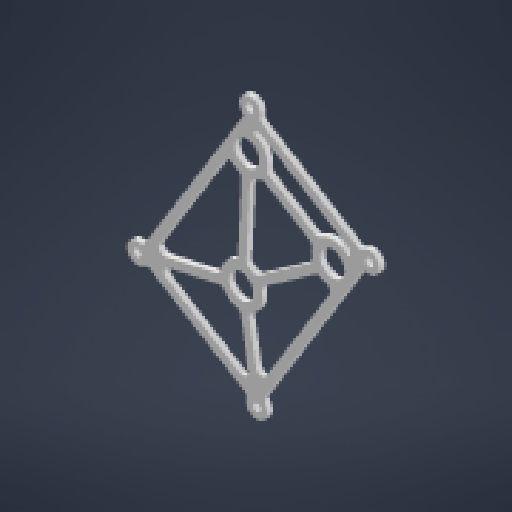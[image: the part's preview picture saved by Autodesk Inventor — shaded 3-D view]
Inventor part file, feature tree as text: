
AUTODESK INVENTOR PART (.ipt)
format: ipt  version: 2024.2 (Build 282272000, 272)  size: 302,592 bytes
history: native  units: in
note: dims shown in document units (in); Inventor stores cm internally (conversion verified against a paired STEP export)
features: reference x8, other x7, extrude x2, sketch x2, fillet x1, projected_geometry x1
ambient origin geometry x8: Origin, YZ Plane, XZ Plane, XY Plane, X Axis, Y Axis, Z Axis, Center Point
bodies: Solid1 (feature_tree)
feature tree (21):
  extrude  "Extrusion1"  Depth=0.7in
  fillet  "Fillet1"  Radius=0.7in
  extrude  "Extrusion2"  Depth=0.125in
  sketch  "Sketch1"  dims[d0=0.1693in d1=0.7in d2=0.7in]
  reference  "Reference1"
  reference  "Reference2"
  reference  "Reference3"
  reference  "Reference4"
  reference  "Reference5"
  reference  "Reference6"
  reference  "Reference7"
  reference  "Reference8"
  sketch  "Sketch2"  dims[d3=0.1693in d4=0.1693in d5=0.1693in d6=1.593in d7=0.4724in d8=0.4724in d9=0.4724in d10=0.4724in d11=0.125in d12=0.0in d13=0.125in d14=0.2in d15=0.2in d16=0.2in d17=0.2in d18=0.2in d19=0.2in d20=0.2in d21=0.2in d22=0.125in d23=0.2in d25=0.125in d26=0.125in d27=0.125in d28=0.2in d29=0.125in d30=0.125in d31=0.125in d32=0.125in d33=0.2in d34=0.125in d35=0.2in d36=0.125in d37=0.125in d38=1.0in d39=0.0in]
  other  "<userpath>\Desktop\Robotics\Swerve2\Assemblies\Pod.iam"
  other  "Pod.iam"
  other  "2800 Series Zinc-Plated Steel Socket Head Screw (M4 x 0.7mm, 7mm Length) - 25 Pack:7"
  other  "2800 Series Zinc-Plated Steel Socket Head Screw (M4 x 0.7mm, 7mm Length) - 25 Pack:5"
  other  "2800 Series Zinc-Plated Steel Socket Head Screw (M4 x 0.7mm, 12mm Length) - 25 Pack:2"
  other  "2800 Series Zinc-Plated Steel Socket Head Screw (M4 x 0.7mm, 12mm Length) - 25 Pack:1"
  other  "Lower_Plate:1"
  projected_geometry  "Project Cut Edges1"
